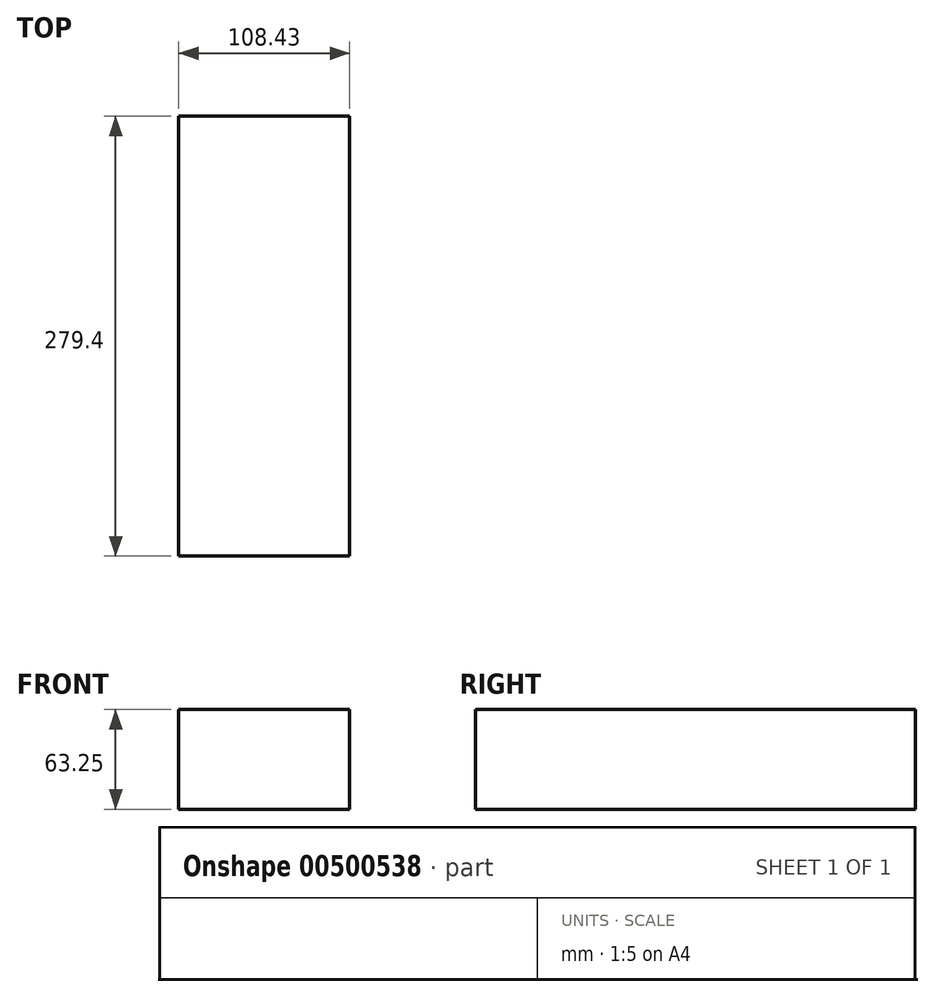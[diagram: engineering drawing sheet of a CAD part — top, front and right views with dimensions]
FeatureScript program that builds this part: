
annotation { "Feature Type Name" : "Feature", "Feature Type Description" : "" }
export const myFeature = defineFeature(function(context is Context, id is Id, definition is map)
    precondition{}
    {
        {
            var Q0;
            Q0=qCreatedBy(makeId("Front.planeOp"),FACE);
            var sketch = newSketch(context, id + "F0", { "sketchPlane" : qUnion([Q0])});
            skLineSegment(sketch, "E0.bottom", {"start": v(-57.42, 27.84) * mm, "end": v(51, 27.84) * mm});
            skLineSegment(sketch, "E0.top", {"start": v(-57.42, -35.41) * mm, "end": v(51, -35.41) * mm});
            skLineSegment(sketch, "E0.left", {"start": v(-57.42, 27.84) * mm, "end": v(-57.42, -35.41) * mm});
            skLineSegment(sketch, "E0.right", {"start": v(51, 27.84) * mm, "end": v(51, -35.41) * mm});
            skSolve(sketch);
        }
        {
            var Q0;
            Q0=makeQuery(id+"F0.imprint","IMPRINT",FACE,{"disambiguationData":[TD([[makeQuery(id+"F0.imprint","IMPRINT",EDGE,{"derivedFrom":sQuery(id+"F0.wireOp",EDGE,"E0.bottom")}),-1.0]])]});
            extrude(context, id + "F1", {"entities" : qUnion([Q0]), "depth" : 279.4 * mm});
        }
    });
